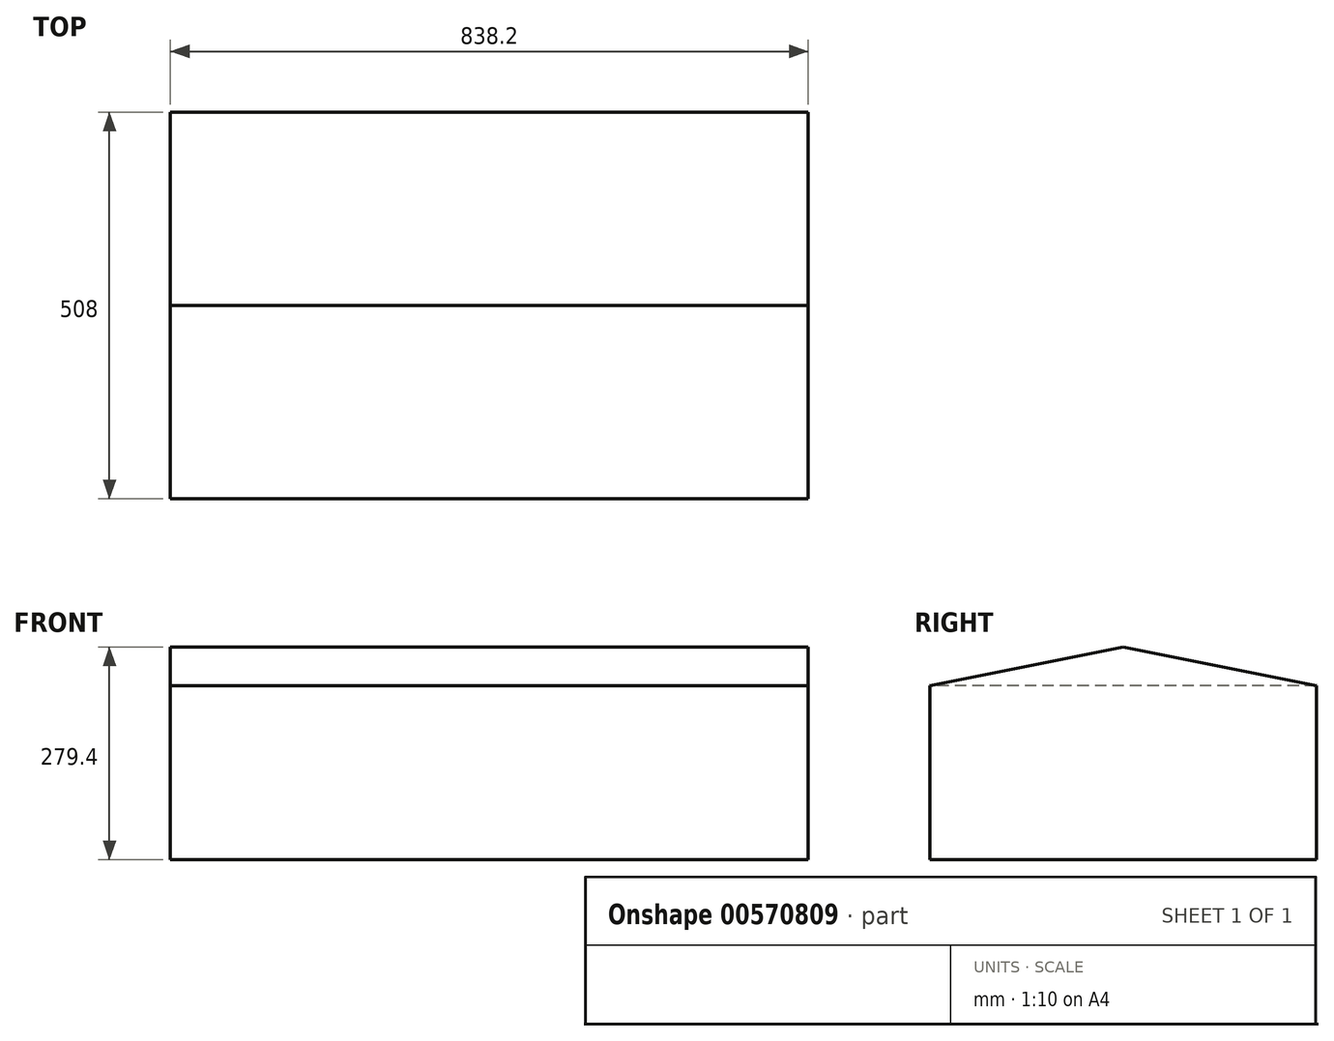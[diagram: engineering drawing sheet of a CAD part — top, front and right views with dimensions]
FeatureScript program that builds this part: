
annotation { "Feature Type Name" : "Feature", "Feature Type Description" : "" }
export const myFeature = defineFeature(function(context is Context, id is Id, definition is map)
    precondition{}
    {
        {
            var Q0;
            Q0=qCreatedBy(makeId("Top.planeOp"),FACE);
            var sketch = newSketch(context, id + "F0", { "sketchPlane" : qUnion([Q0])});
            skLineSegment(sketch, "E0.bottom", {"start": v(-678.59, 372.17) * mm, "end": v(159.61, 372.17) * mm});
            skLineSegment(sketch, "E0.top", {"start": v(-678.59, -135.83) * mm, "end": v(159.61, -135.83) * mm});
            skLineSegment(sketch, "E0.left", {"start": v(-678.59, 372.17) * mm, "end": v(-678.59, -135.83) * mm});
            skLineSegment(sketch, "E0.right", {"start": v(159.61, 372.17) * mm, "end": v(159.61, -135.83) * mm});
            skLineSegment(sketch, "E1.bottom", {"start": v(83.41, -59.63) * mm, "end": v(-602.39, -59.63) * mm});
            skLineSegment(sketch, "E1.top", {"start": v(83.41, 295.97) * mm, "end": v(-602.39, 295.97) * mm});
            skLineSegment(sketch, "E1.left", {"start": v(83.41, -59.63) * mm, "end": v(83.41, 295.97) * mm});
            skLineSegment(sketch, "E1.right", {"start": v(-602.39, -59.63) * mm, "end": v(-602.39, 295.97) * mm});
            skSolve(sketch);
        }
        {
            var Q0;
            Q0=makeQuery(id+"F0.imprint","IMPRINT",FACE,{"disambiguationData":[TD([[makeQuery(id+"F0.imprint","IMPRINT",EDGE,{"derivedFrom":sQuery(id+"F0.wireOp",EDGE,"E1.bottom")}),-1.0]])]});
            var Q1;
            Q1=makeQuery(id+"F0.imprint","IMPRINT",FACE,{"disambiguationData":[TD([[makeQuery(id+"F0.imprint","IMPRINT",EDGE,{"derivedFrom":sQuery(id+"F0.wireOp",EDGE,"E0.bottom")}),-1.0]])]});
            extrude(context, id + "F1", {"entities" : qUnion([Q0, Q1]), "depth" : 228.6 * mm, "offsetDistance" : 25.4 * mm});
        }
        {
            var Q0;
            Q0=makeQuery(id+"F1.opExtrude","CAP_FACE",FACE,{"disambiguationData":[OSD([sQuery(id+"F0.wireOp",EDGE,"E0.bottom"),sQuery(id+"F0.wireOp",EDGE,"E0.top"),sQuery(id+"F0.wireOp",EDGE,"E0.left"),sQuery(id+"F0.wireOp",EDGE,"E0.right")])],"isStart":true});
            shell(context, id + "F2", {"entities" : qUnion([Q0]), "thickness" : 0.25 * mm});
        }
        {
            var Q0;
            Q0=makeQuery(id+"F1.opExtrude","SWEPT_FACE",FACE,{"disambiguationData":[OSD([sQuery(id+"F0.wireOp",EDGE,"E0.right")])]});
            var sketch = newSketch(context, id + "F3", { "sketchPlane" : qUnion([Q0])});
            skLineSegment(sketch, "E2", {"start": v(-135.83, 228.6) * mm, "end": v(118.17, 228.6) * mm});
            skLineSegment(sketch, "E3", {"start": v(118.17, 228.6) * mm, "end": v(118.17, 279.4) * mm});
            skLineSegment(sketch, "E4", {"start": v(-135.83, 228.6) * mm, "end": v(118.17, 279.4) * mm});
            skLineSegment(sketch, "E5", {"start": v(372.17, 228.6) * mm, "end": v(118.17, 279.4) * mm});
            skSolve(sketch);
        }
        {
            var Q0;
            Q0 = qSketchRegion(id + "F3", true);
            var Q1;
            {var subQ0=sQuery(id+"F3.wireOp",EDGE,"E3");Q1=makeQuery(id+"F3.imprint","IMPRINT",FACE,{"disambiguationData":[TD([[makeQuery(id+"F3.imprint","IMPRINT",EDGE,{"derivedFrom":subQ0}),-1.0]])]});}
            extrude(context, id + "F4", {"entities" : qUnion([Q0, Q1]), "operationType" : NewBodyOperationType.ADD, "oppositeDirection" : true, "depth" : 838.2 * mm, "offsetDistance" : 25.4 * mm});
        }
    });
